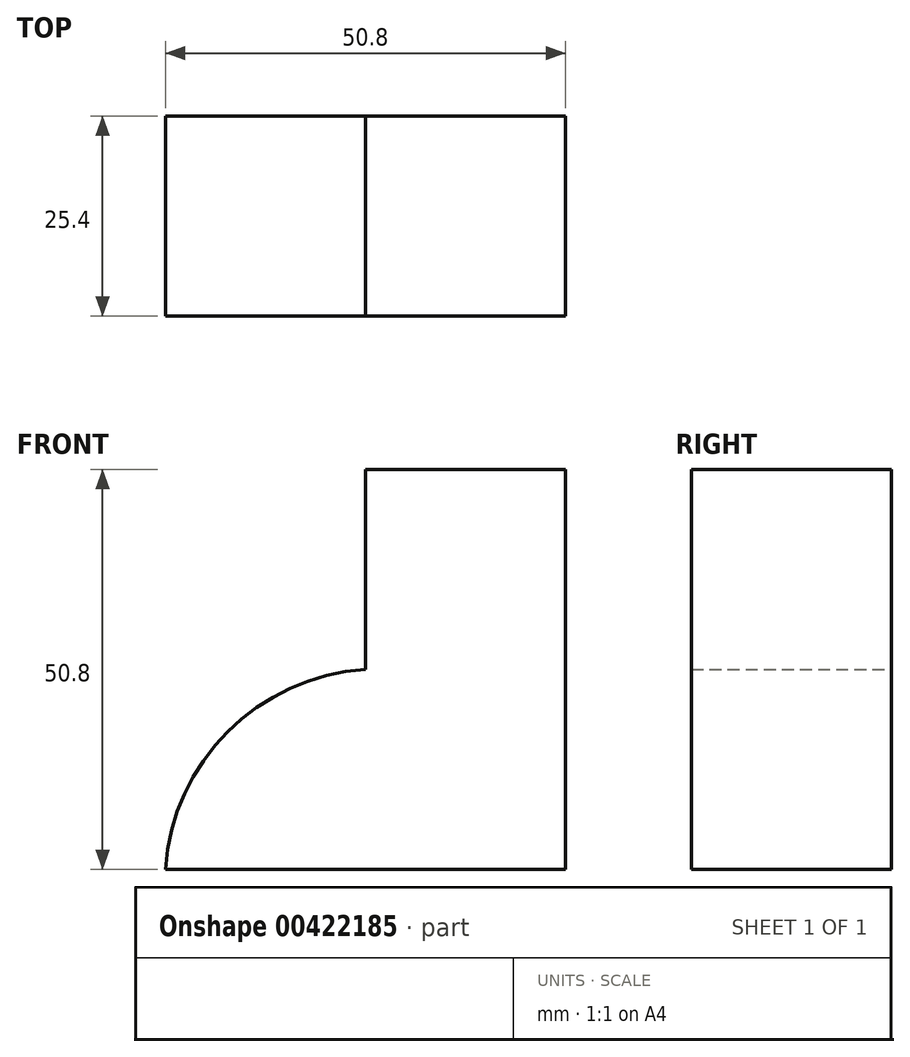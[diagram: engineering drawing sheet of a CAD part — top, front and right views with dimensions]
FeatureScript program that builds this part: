
annotation { "Feature Type Name" : "Feature", "Feature Type Description" : "" }
export const myFeature = defineFeature(function(context is Context, id is Id, definition is map)
    precondition{}
    {
        {
            var Q0;
            Q0=qCreatedBy(makeId("Front.planeOp"),FACE);
            var sketch = newSketch(context, id + "F0", { "sketchPlane" : qUnion([Q0])});
            skLineSegment(sketch, "E0", {"start": v(45.84, 6.5) * mm, "end": v(45.84, -44.3) * mm});
            skLineSegment(sketch, "E1", {"start": v(45.84, -44.3) * mm, "end": v(-4.96, -44.3) * mm});
            skLineSegment(sketch, "E2", {"start": v(45.84, 6.5) * mm, "end": v(20.44, 6.5) * mm});
            skLineSegment(sketch, "E3", {"start": v(20.44, 6.5) * mm, "end": v(20.44, -18.9) * mm});
            skArc(sketch, "E4", {"start": v(20.44, -18.9) * mm, "mid": v(2.94, -26.8) * mm, "end": v(-4.96, -44.3) * mm});
            skSolve(sketch);
        }
        {
            var Q0;
            Q0=makeQuery(id+"F0.imprint","IMPRINT",FACE,{"disambiguationData":[TD([[makeQuery(id+"F0.imprint","IMPRINT",EDGE,{"derivedFrom":sQuery(id+"F0.wireOp",EDGE,"E0")}),-1.0]])]});
            extrude(context, id + "F1", {"entities" : qUnion([Q0]), "depth" : 25.4 * mm});
        }
    });
